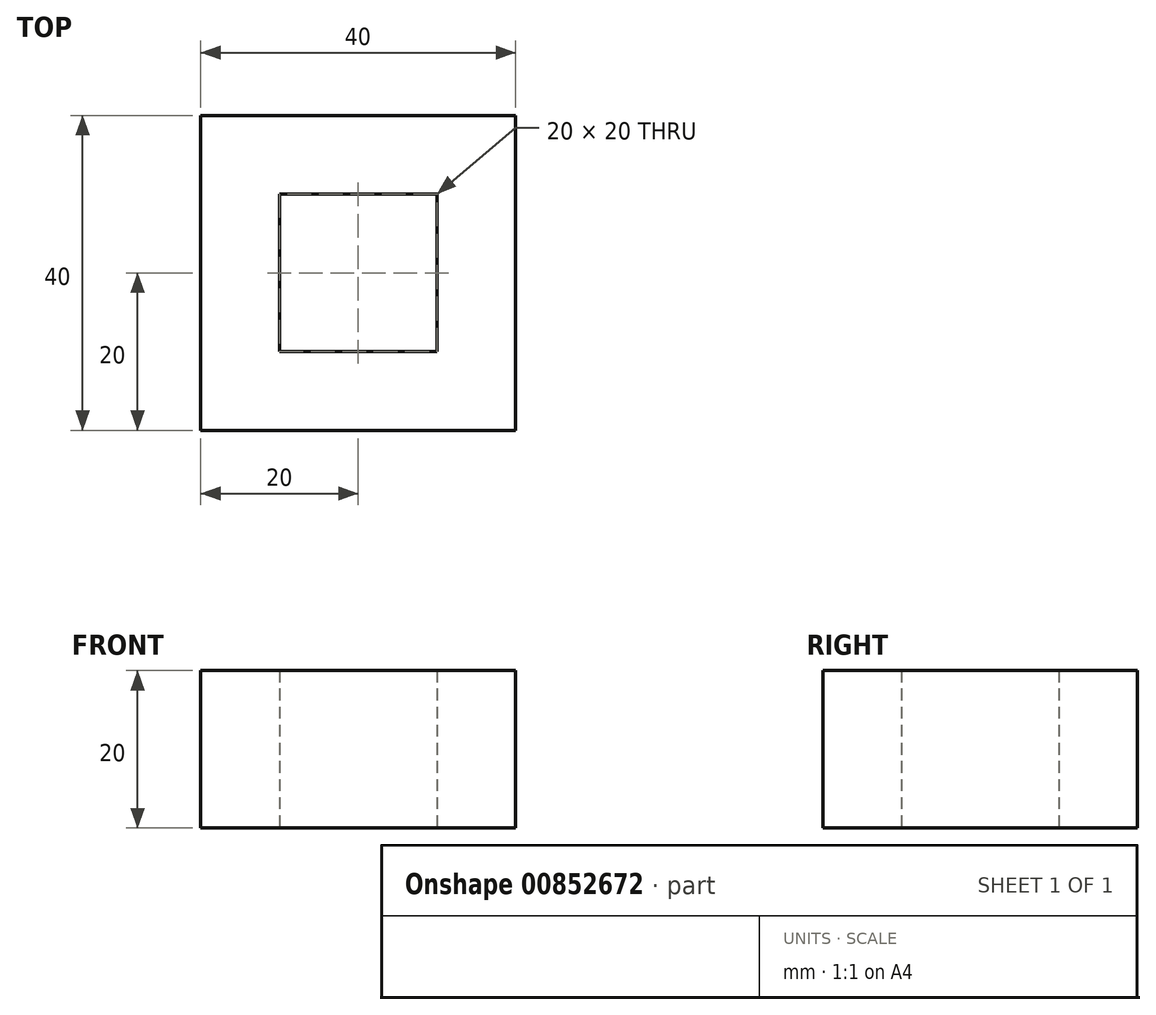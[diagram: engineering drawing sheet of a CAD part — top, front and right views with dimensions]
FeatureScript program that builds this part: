
annotation { "Feature Type Name" : "Feature", "Feature Type Description" : "" }
export const myFeature = defineFeature(function(context is Context, id is Id, definition is map)
    precondition{}
    {
        {
            var Q0;
            Q0=qCreatedBy(makeId("Top.planeOp"),FACE);
            var sketch = newSketch(context, id + "F0", { "sketchPlane" : qUnion([Q0])});
            skLineSegment(sketch, "E0.bottom", {"start": v(0, 0) * mm, "end": v(40, 0) * mm});
            skLineSegment(sketch, "E0.top", {"start": v(0, 40) * mm, "end": v(40, 40) * mm});
            skLineSegment(sketch, "E0.left", {"start": v(0, 0) * mm, "end": v(0, 40) * mm});
            skLineSegment(sketch, "E0.right", {"start": v(40, 0) * mm, "end": v(40, 40) * mm});
            skLineSegment(sketch, "E1.bottom", {"start": v(10, 10) * mm, "end": v(30, 10) * mm});
            skLineSegment(sketch, "E1.top", {"start": v(10, 30) * mm, "end": v(30, 30) * mm});
            skLineSegment(sketch, "E1.left", {"start": v(10, 10) * mm, "end": v(10, 30) * mm});
            skLineSegment(sketch, "E1.right", {"start": v(30, 10) * mm, "end": v(30, 30) * mm});
            skLineSegment(sketch, "E2", {"start": v(0, 0) * mm, "end": v(40, 40) * mm, "construction": true});
            skLineSegment(sketch, "E3", {"start": v(0, 40) * mm, "end": v(40, 0) * mm, "construction": true});
            skSolve(sketch);
        }
        {
            var Q0;
            Q0 = qSketchRegion(id + "F0", true);
            extrude(context, id + "F1", {"entities" : qUnion([Q0]), "depth" : 20 * mm, "offsetDistance" : 25 * mm});
        }
    });
